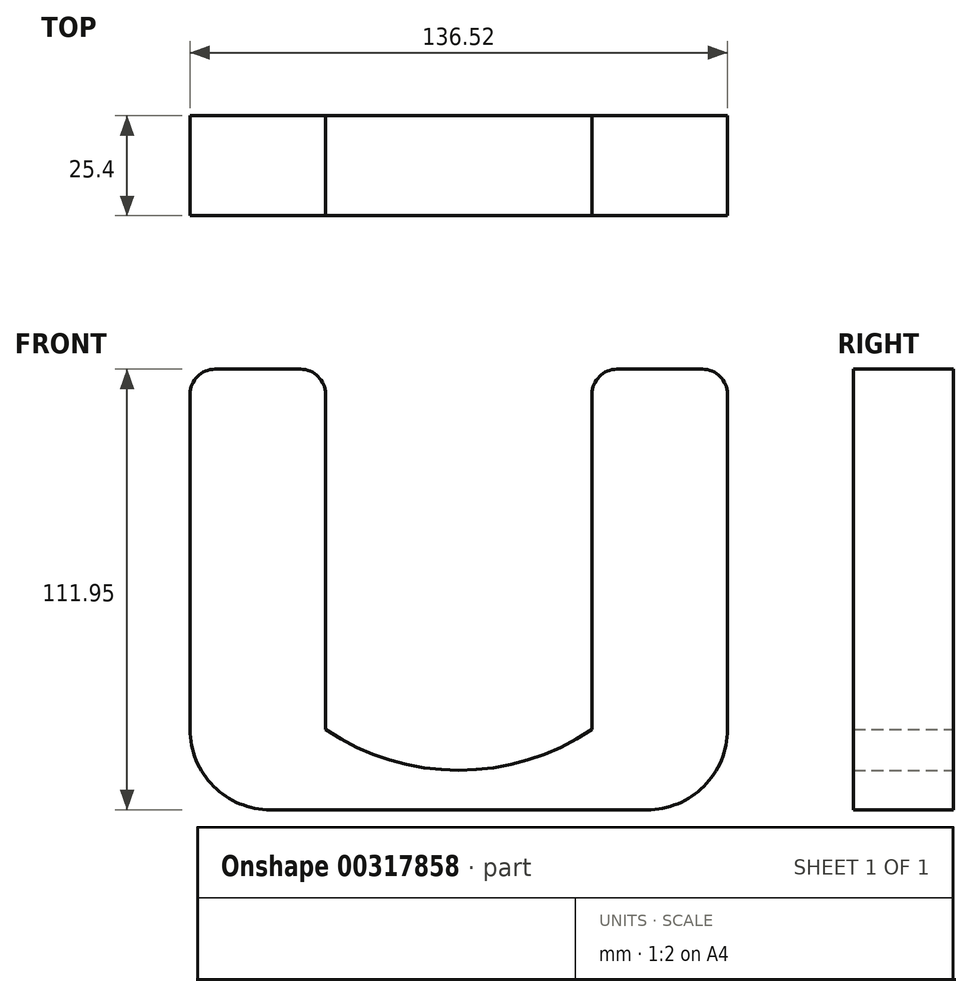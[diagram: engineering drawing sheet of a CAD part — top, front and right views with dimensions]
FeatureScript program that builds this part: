
annotation { "Feature Type Name" : "Feature", "Feature Type Description" : "" }
export const myFeature = defineFeature(function(context is Context, id is Id, definition is map)
    precondition{}
    {
        {
            var Q0;
            Q0=qCreatedBy(makeId("Front.planeOp"),FACE);
            var sketch = newSketch(context, id + "F0", { "sketchPlane" : qUnion([Q0])});
            skLineSegment(sketch, "E0.bottom", {"start": v(-33.87, -15.57) * mm, "end": v(-68.26, -15.57) * mm});
            skLineSegment(sketch, "E0.top", {"start": v(-40.22, 75.98) * mm, "end": v(-61.91, 75.98) * mm});
            skLineSegment(sketch, "E0.left", {"start": v(-33.87, -15.57) * mm, "end": v(-33.87, 69.63) * mm});
            skLineSegment(sketch, "E0.right", {"start": v(-68.26, -15.57) * mm, "end": v(-68.26, 69.63) * mm});
            skPoint(sketch, "E0.middle", {"position": v(-51.07, 30.2) * mm});
            skArc(sketch, "E1", {"start": v(-68.26, -15.57) * mm, "mid": v(-62.27, -30.01) * mm, "end": v(-47.81, -35.97) * mm});
            skArc(sketch, "E2", {"start": v(-33.87, -15.57) * mm, "mid": v(-17.7, -23.28) * mm, "end": v(0, -25.92) * mm});
            skLineSegment(sketch, "E3", {"start": v(-47.81, -35.97) * mm, "end": v(0, -35.97) * mm});
            skPoint(sketch, "E4", {"position": v(-23.9, -35.97) * mm});
            skLineSegment(sketch, "E5.MirrorCS", {"start": v(40.22, 75.98) * mm, "end": v(61.91, 75.98) * mm});
            skLineSegment(sketch, "E6.MirrorCS", {"start": v(33.87, -15.57) * mm, "end": v(33.87, 69.63) * mm});
            skLineSegment(sketch, "E7.MirrorCS", {"start": v(33.87, -15.57) * mm, "end": v(68.26, -15.57) * mm});
            skLineSegment(sketch, "E8.MirrorCS", {"start": v(47.81, -35.97) * mm, "end": v(0, -35.97) * mm});
            skLineSegment(sketch, "E9.MirrorCS", {"start": v(68.26, -15.57) * mm, "end": v(68.26, 69.63) * mm});
            skArc(sketch, "E10.MirrorCS", {"start": v(68.26, -15.57) * mm, "mid": v(62.27, -30.01) * mm, "end": v(47.81, -35.97) * mm});
            skArc(sketch, "E11.MirrorCS", {"start": v(33.87, -15.57) * mm, "mid": v(17.7, -23.28) * mm, "end": v(0, -25.92) * mm});
            skPoint(sketch, "E12.visualSharp", {"position": v(-68.26, 75.98) * mm});
            skArc(sketch, "E12.filletArc", {"start": v(-61.91, 75.98) * mm, "mid": v(-66.4, 74.12) * mm, "end": v(-68.26, 69.63) * mm});
            skPoint(sketch, "E13.visualSharp", {"position": v(-33.87, 75.98) * mm});
            skArc(sketch, "E13.filletArc", {"start": v(-33.87, 69.63) * mm, "mid": v(-35.73, 74.12) * mm, "end": v(-40.22, 75.98) * mm});
            skPoint(sketch, "E14.visualSharp", {"position": v(33.87, 75.98) * mm});
            skArc(sketch, "E14.filletArc", {"start": v(40.22, 75.98) * mm, "mid": v(35.73, 74.12) * mm, "end": v(33.87, 69.63) * mm});
            skPoint(sketch, "E15.visualSharp", {"position": v(68.26, 75.98) * mm});
            skArc(sketch, "E15.filletArc", {"start": v(68.26, 69.63) * mm, "mid": v(66.4, 74.12) * mm, "end": v(61.91, 75.98) * mm});
            skSolve(sketch);
        }
        {
            var Q0;
            Q0 = qSketchRegion(id + "F0", true);
            extrude(context, id + "F1", {"entities" : qUnion([Q0]), "depth" : 25.4 * mm});
        }
        {
            var Q0;
            Q0=makeQuery(id+"F1.opExtrude","CAP_FACE",FACE,{"disambiguationData":[OSD([sQuery(id+"F0.wireOp",EDGE,"E0.top"),sQuery(id+"F0.wireOp",EDGE,"E0.left"),sQuery(id+"F0.wireOp",EDGE,"E0.right"),sQuery(id+"F0.wireOp",EDGE,"E1"),sQuery(id+"F0.wireOp",EDGE,"E2"),sQuery(id+"F0.wireOp",EDGE,"E3"),sQuery(id+"F0.wireOp",EDGE,"E5.MirrorCS"),sQuery(id+"F0.wireOp",EDGE,"E6.MirrorCS"),sQuery(id+"F0.wireOp",EDGE,"E8.MirrorCS"),sQuery(id+"F0.wireOp",EDGE,"E9.MirrorCS"),sQuery(id+"F0.wireOp",EDGE,"E10.MirrorCS"),sQuery(id+"F0.wireOp",EDGE,"E11.MirrorCS"),sQuery(id+"F0.wireOp",EDGE,"E12.filletArc"),sQuery(id+"F0.wireOp",EDGE,"E13.filletArc"),sQuery(id+"F0.wireOp",EDGE,"E14.filletArc"),sQuery(id+"F0.wireOp",EDGE,"E15.filletArc")])],"isStart":false});
            var sketch = newSketch(context, id + "F2", { "sketchPlane" : qUnion([Q0])});
            skCircle(sketch, "E16", {"center": v(-51.74, 8.07) * mm, "radius": 9.88 * mm});
            skCircle(sketch, "E17.MirrorC", {"center": v(51.74, 8.07) * mm, "radius": 9.88 * mm});
            skSolve(sketch);
        }
        {
            var Q0;
            Q0=sQuery(id+"F2.wireOp",EDGE,"E16");
            var Q1;
            Q1=sQuery(id+"F2.wireOp",EDGE,"E17.MirrorC");
            extrude(context, id + "F3", {"bodyType" : ToolBodyType.SURFACE, "surfaceEntities" : qUnion([Q0, Q1]), "depth" : 12.7 * mm});
        }
    });
